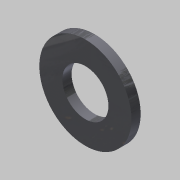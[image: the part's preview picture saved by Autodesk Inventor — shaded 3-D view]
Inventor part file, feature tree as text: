
AUTODESK INVENTOR PART (.ipt)
format: ipt  version: 2013 (Build 170138000, 138)  size: 79,872 bytes
history: native  units: in
note: dims shown in document units (in); Inventor stores cm internally (conversion verified against a paired STEP export)
features: extrude x1, sketch x1
ambient origin geometry x8: Origin, YZ Plane, XZ Plane, XY Plane, X Axis, Y Axis, Z Axis, Center Point
bodies: Solid1 (feature_tree)
feature tree (2):
  extrude  "Extrusion1"  Depth=0.3937in
  sketch  "Sketch1"  dims[d0=0.1969in d1=0.3937in d2=0.0394in d3=0.0in]
